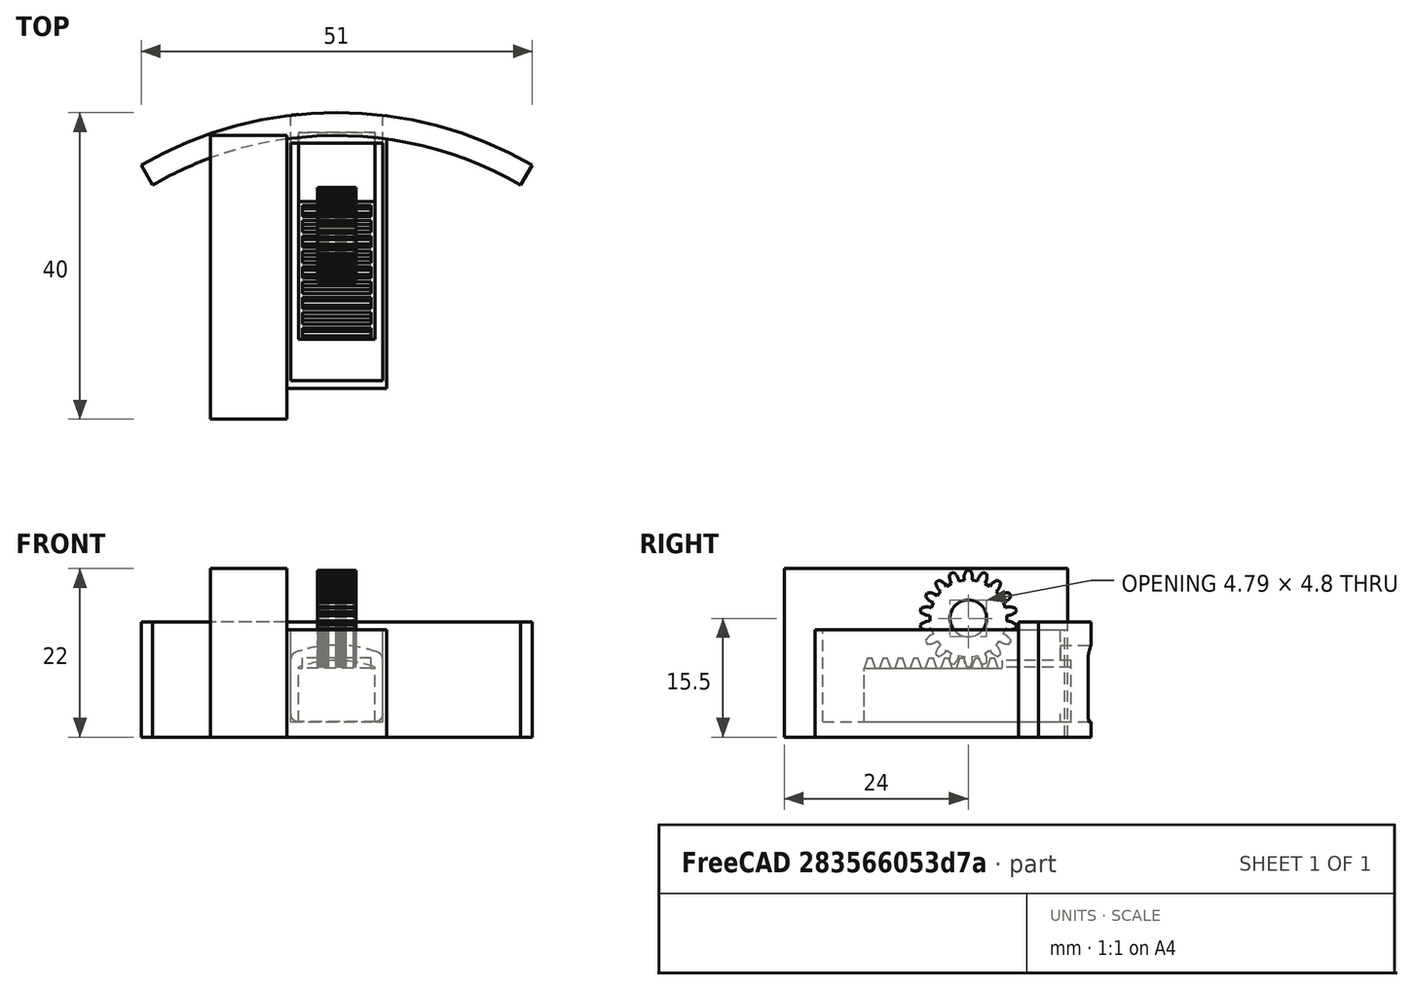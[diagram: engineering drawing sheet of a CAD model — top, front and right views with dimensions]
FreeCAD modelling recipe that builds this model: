
FCSTD DOCUMENT  (FreeCAD 0.16R4924 (Git))
Label: interior_servo_bay_v4p11
License: All rights reserved
LicenseURL: http://en.wikipedia.org/wiki/All_rights_reserved
objects: Part::Feature×11, Part::Box×6, Part::Cut×5, Part::MultiFuse×4, Part::Cylinder×3, Part::Extrusion×3, Part::Thickness×1, Mesh::Feature×1, Part::Fuse×1, Part::FeaturePython×1, Part::Prism×1, Part::MultiCommon×1
note: 37 computed .brp shape members not serialized (recipe doc carries the construction recipe); baked Part::Feature solids carry a one-line shape summary decoded from their .brp

FEATURE [Part::Cylinder] Cylinder  label="bottle_wall"
  Angle = 60
  Height = 15
  Placement = pos=(8.5,-7,0) rot=(0,0,1;1.0472rad)
  Radius = 51
FEATURE [Part::Cylinder] Cylinder001  label="bottle_wall001"
  Angle = 60
  Height = 15
  Placement = pos=(8.5,-7,0) rot=(0,0,1;1.0472rad)
  Radius = 48
FEATURE [Part::Cut] Cut  label="bottle_wall_composite"
  Base = -> Cylinder
  Placement = pos=(0,-2,0) rot=(0,0,1;0rad)
  Tool = -> Cylinder001
FEATURE [Part::Feature] Common_cs  label="pin_cs"
  Placement = pos=(3.5,35,2) rot=(0,0,1;0rad)
  shape: bbox 10 x 2e-07 x 8 mm, 0 faces, 0 solids (baked)
FEATURE [Part::Extrusion] Extrude
  Base = -> Common_cs
  Dir = (0,5,0)
  Solid = true
FEATURE [Part::Thickness] Thickness
  Faces = -> Extrude [Face7]
  Intersection = false
  Join = 0
  Mode = 0
  SelfIntersection = false
  Value = 1
FEATURE [Part::Feature] Common_cs001  label="pin_cs001"
  Placement = pos=(3.5,35,2) rot=(0,0,1;0rad)
  shape: bbox 10 x 2e-07 x 8 mm, 0 faces, 0 solids (baked)
FEATURE [Part::Extrusion] Extrude001
  Base = -> Common_cs001
  Dir = (0,5,0)
  Solid = true
FEATURE [Part::MultiFuse] Fusion  label="bolt_bottle_side_opening"
  Placement = pos=(0,-7,1) rot=(0,0,1;0rad)
  Shapes = -> [Thickness,Extrude,Extrude001]
FEATURE [Part::Box] Box  label="pullBay"
  Height = 15
  Length = 12
  Placement = pos=(2.5,7,2) rot=(0,0,1;0rad)
  Width = 31
FEATURE [Part::Box] Box001  label="Case"
  Height = 14
  Length = 13
  Placement = pos=(2,6,0) rot=(0,0,1;0rad)
  Width = 34
FEATURE [Part::Cut] Cut001  label="cut bay from case"
  Base = -> Box001
  Tool = -> Box
FEATURE [Part::MultiFuse] Fusion001  label="wall plus case"
  Shapes = -> [Cut,Cut001]
FEATURE [Part::Cut] Cut002  label="hole cut out of case"
  Base = -> Fusion001
  Tool = -> Fusion
FEATURE [Mesh::Feature] Mesh  label="servo_motor_2"
  Placement = pos=(33.6,-52,22) rot=(0,0,-1;1.5708rad)
FEATURE [Part::Fuse] union  label="pinion"
FEATURE [Part::FeaturePython] RefineLinearExtrude  # WARN: FeaturePython — macro-defined, semantics opaque (R4)
  Base = -> union
FEATURE [Part::Extrusion] LinearExtrude
  Base = -> RefineLinearExtrude
  Dir = (0,0,5)
  Solid = true
FEATURE [Part::Prism] prism
  Circumradius = 2.4
  Height = 7
  Placement = pos=(0,0,-1) rot=(0,0,1;0rad)
  Polygon = 50
FEATURE [Part::Cut] difference  label="pinion_final"
  Base = -> LinearExtrude
  Placement = pos=(6,26,15.5) rot=(0,1,0;1.5708rad)
  Tool = -> prism
FEATURE [Part::Cylinder] Cylinder002  label="rounded_top"
  Angle = 360
  Height = 40
  Placement = pos=(5,35,-7) rot=(1,0,0;1.5708rad)
  Radius = 15
FEATURE [Part::Box] Box005  label="pin"
  Height = 8
  Length = 10
  Width = 27
FEATURE [Part::MultiCommon] Common  label="rounded pin"
  Shapes = -> [Cylinder002,Box005]
FEATURE [Part::Box] Box006  label="flat_top"
  Height = 10
  Length = 10
  Placement = pos=(0,0,7) rot=(0,0,1;0rad)
  Width = 18
FEATURE [Part::Cut] Cut005
  Base = -> Common
  Placement = pos=(0,11,0) rot=(0,0,1;0rad)
  Tool = -> Box006
FEATURE [Part::Box] cube
  Height = 5
  Length = 18
  Placement = pos=(-12,-4.5,-2.5) rot=(0,0,1;0rad)
  Width = 9
FEATURE [Part::Feature] polyhedron
  Placement = pos=(-11.2451,0,2.5) rot=(0,0,1;0rad)
  shape: bbox 1.51 x 9 x 1.337 mm, 6 faces (baked)
FEATURE [Part::Feature] polyhedron001
  Placement = pos=(-9.24512,0,2.5) rot=(0,0,1;0rad)
  shape: bbox 1.51 x 9 x 1.337 mm, 6 faces (baked)
FEATURE [Part::Feature] polyhedron002
  Placement = pos=(-7.24512,0,2.5) rot=(0,0,1;0rad)
  shape: bbox 1.51 x 9 x 1.337 mm, 6 faces (baked)
FEATURE [Part::Feature] polyhedron003
  Placement = pos=(-5.24512,0,2.5) rot=(0,0,1;0rad)
  shape: bbox 1.51 x 9 x 1.337 mm, 6 faces (baked)
FEATURE [Part::Feature] polyhedron004
  Placement = pos=(-3.24512,0,2.5) rot=(0,0,1;0rad)
  shape: bbox 1.51 x 9 x 1.337 mm, 6 faces (baked)
FEATURE [Part::Feature] polyhedron005
  Placement = pos=(-1.24512,0,2.5) rot=(0,0,1;0rad)
  shape: bbox 1.51 x 9 x 1.337 mm, 6 faces (baked)
FEATURE [Part::Feature] polyhedron006
  Placement = pos=(0.754882,0,2.5) rot=(0,0,1;0rad)
  shape: bbox 1.51 x 9 x 1.337 mm, 6 faces (baked)
FEATURE [Part::Feature] polyhedron007
  Placement = pos=(2.75488,0,2.5) rot=(0,0,1;0rad)
  shape: bbox 1.51 x 9 x 1.337 mm, 6 faces (baked)
FEATURE [Part::Feature] polyhedron008
  Placement = pos=(4.75488,0,2.5) rot=(0,0,1;0rad)
  shape: bbox 1.51 x 9 x 1.337 mm, 6 faces (baked)
FEATURE [Part::MultiFuse] Fusion003  label="rack"
  Placement = pos=(5,23,4.5) rot=(0,0,1;1.5708rad)
  Shapes = -> [cube,polyhedron002,polyhedron003,polyhedron004,polyhedron005,polyhedron,polyhedron007,polyhedron001,polyhedron006,polyhedron008]
FEATURE [Part::MultiFuse] Fusion004  label="pin_3p2"
  Placement = pos=(3.5,1.4,2) rot=(0,0,1;0rad)
  Shapes = -> [Fusion003,Cut005]
FEATURE [Part::Box] Box007  label="mount"
  Height = 22
  Length = 10
  Placement = pos=(-8,2,0) rot=(0,0,1;0rad)
  Width = 37
